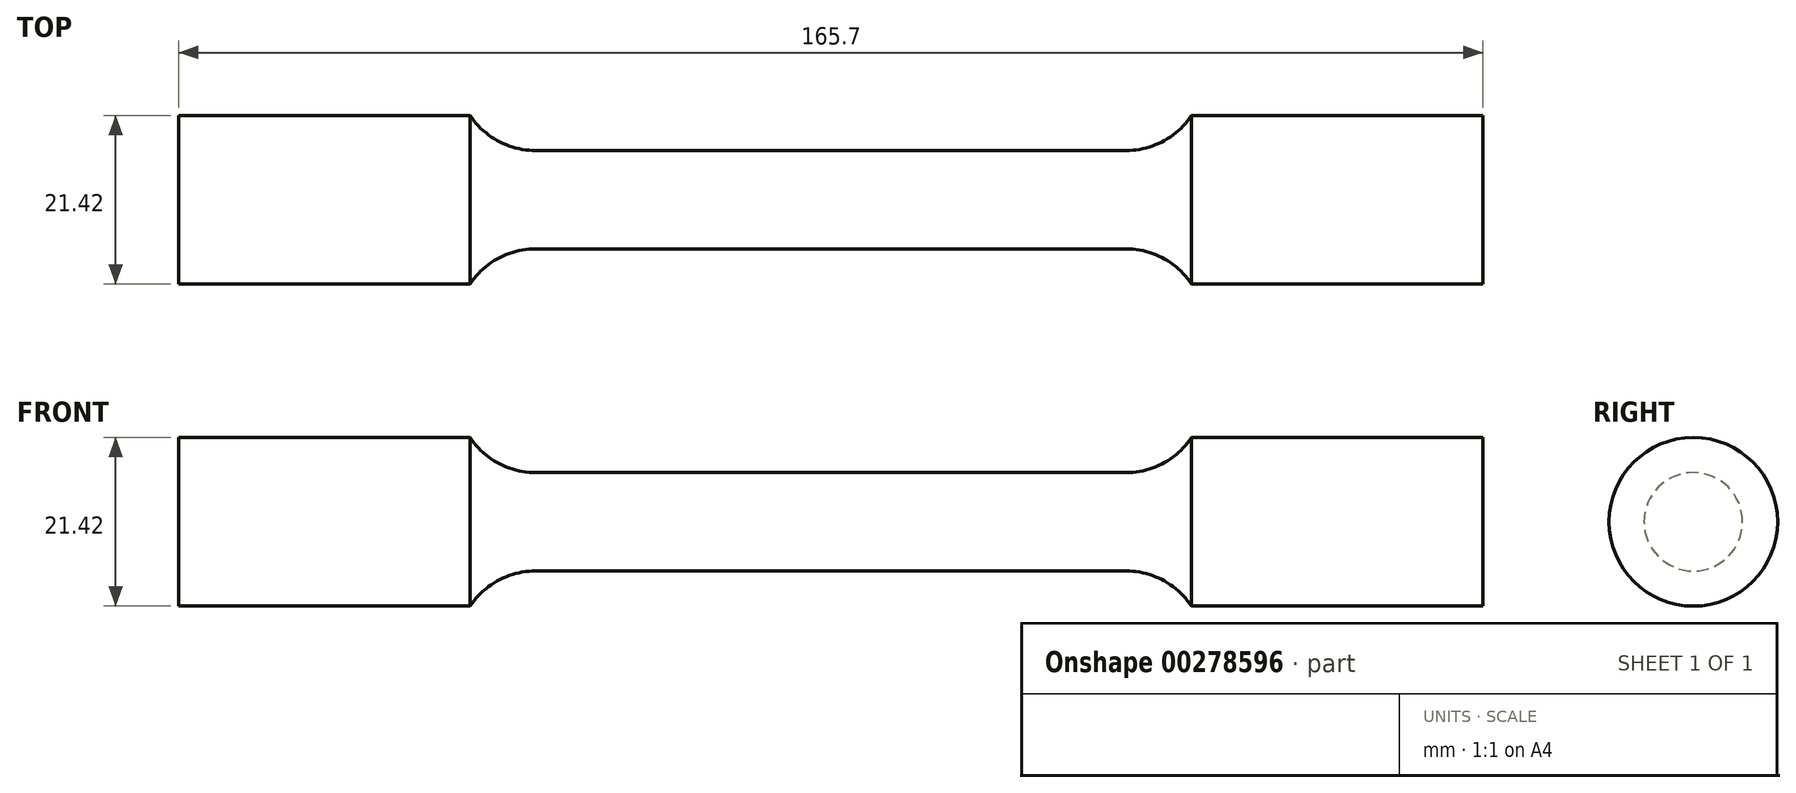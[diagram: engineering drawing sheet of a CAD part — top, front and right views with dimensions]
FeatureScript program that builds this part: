
annotation { "Feature Type Name" : "Feature", "Feature Type Description" : "" }
export const myFeature = defineFeature(function(context is Context, id is Id, definition is map)
    precondition{}
    {
        {
            var Q0;
            Q0=qCreatedBy(makeId("Front.planeOp"),FACE);
            var sketch = newSketch(context, id + "F0", { "sketchPlane" : qUnion([Q0])});
            skLineSegment(sketch, "E0", {"start": v(0, 6.25) * mm, "end": v(37.5, 6.25) * mm});
            skArc(sketch, "E1", {"start": v(37.5, 6.25) * mm, "mid": v(42.22, 7.44) * mm, "end": v(45.83, 10.7) * mm});
            skLineSegment(sketch, "E2", {"start": v(45.83, 10.7) * mm, "end": v(82.85, 10.7) * mm});
            skLineSegment(sketch, "E3", {"start": v(82.85, 10.7) * mm, "end": v(82.85, 0) * mm});
            skLineSegment(sketch, "E4.MirrorCS", {"start": v(0, 6.25) * mm, "end": v(-37.5, 6.25) * mm});
            skArc(sketch, "E5.MirrorCS", {"start": v(-37.5, 6.25) * mm, "mid": v(-42.22, 7.44) * mm, "end": v(-45.83, 10.7) * mm});
            skLineSegment(sketch, "E6.MirrorCS", {"start": v(-82.85, 10.7) * mm, "end": v(-82.85, 0) * mm});
            skLineSegment(sketch, "E7.MirrorCS", {"start": v(-45.83, 10.7) * mm, "end": v(-82.85, 10.7) * mm});
            skLineSegment(sketch, "E8", {"start": v(-82.85, 0) * mm, "end": v(82.85, 0) * mm});
            skSolve(sketch);
        }
        {
            var Q0;
            Q0 = qSketchRegion(id + "F0", true);
            var Q1;
            Q1=sQuery(id+"F0.wireOp",EDGE,"E8");
            revolve(context, id + "F1", {"entities" : qUnion([Q0]), "axis" : qUnion([Q1]), "revolveType" : RevolveType.FULL});
        }
    });
